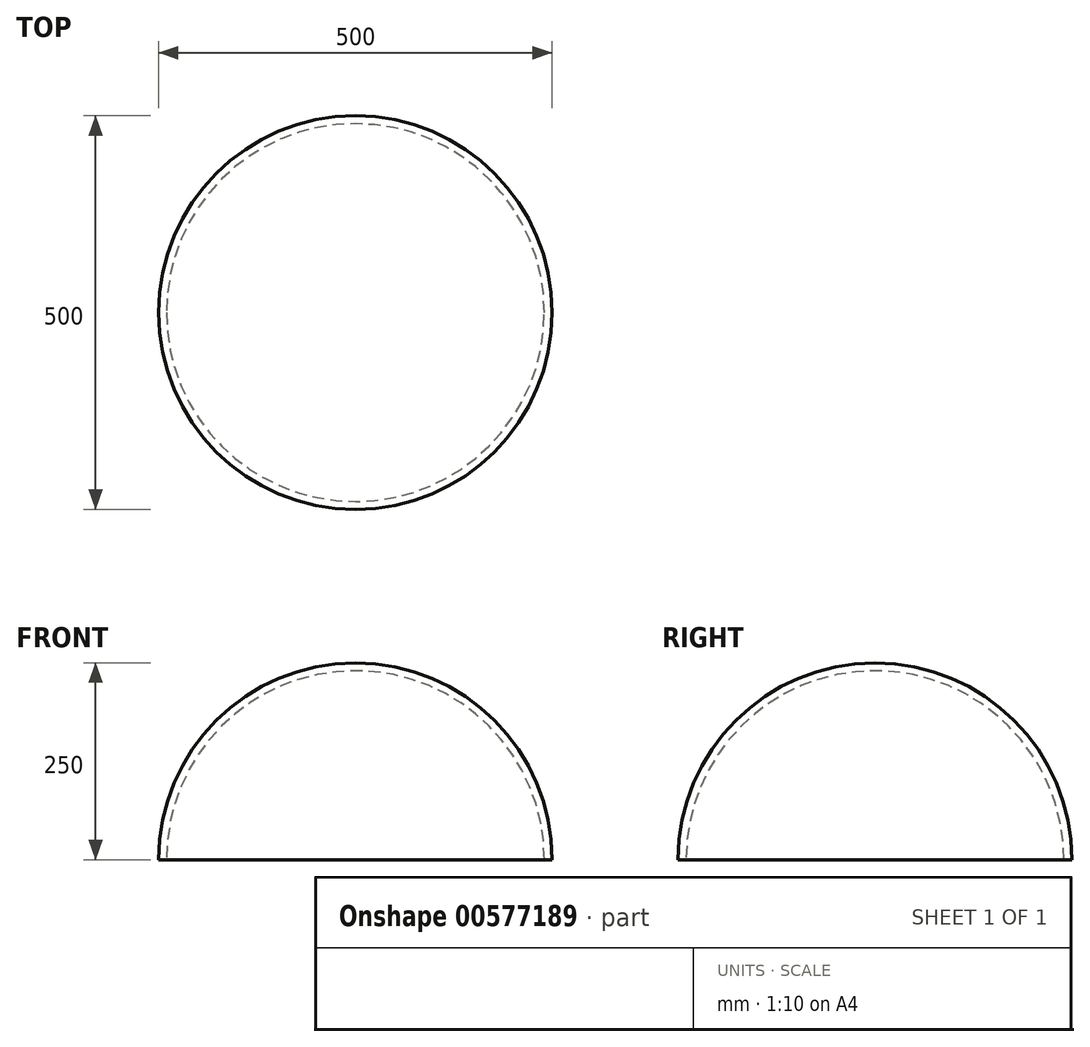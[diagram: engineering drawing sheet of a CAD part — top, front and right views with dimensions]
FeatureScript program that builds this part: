
annotation { "Feature Type Name" : "Feature", "Feature Type Description" : "" }
export const myFeature = defineFeature(function(context is Context, id is Id, definition is map)
    precondition{}
    {
        {
            var Q0;
            Q0=qCreatedBy(makeId("Top.planeOp"),FACE);
            var sketch = newSketch(context, id + "F0", { "sketchPlane" : qUnion([Q0])});
            skArc(sketch, "E0", {"start": v(240, 0) * mm, "mid": v(0, 240) * mm, "end": v(-240, 0) * mm});
            skArc(sketch, "E1", {"start": v(250, 0) * mm, "mid": v(0, 250) * mm, "end": v(-250, 0) * mm});
            skLineSegment(sketch, "E2", {"start": v(-250, 0) * mm, "end": v(-240, 0) * mm});
            skLineSegment(sketch, "E3", {"start": v(240, 0) * mm, "end": v(250, 0) * mm});
            skSolve(sketch);
        }
        {
            var Q0;
            Q0 = qSketchRegion(id + "F0", true);
            var Q1;
            Q1=sQuery(id+"F0.wireOp",EDGE,"E2");
            revolve(context, id + "F1", {"entities" : qUnion([Q0]), "axis" : qUnion([Q1]), "revolveType" : RevolveType.ONE_DIRECTION, "angle" : 180 * degree});
        }
        {
            var Q0;
            Q0=qCreatedBy(makeId("Top.planeOp"),FACE);
            cPlane(context, id + "F2", {"entities" : qUnion([Q0]), "cplaneType" : CPlaneType.OFFSET, "offset" : 300 * mm, "width" : 150 * mm, "height" : 150 * mm});
        }
    });
